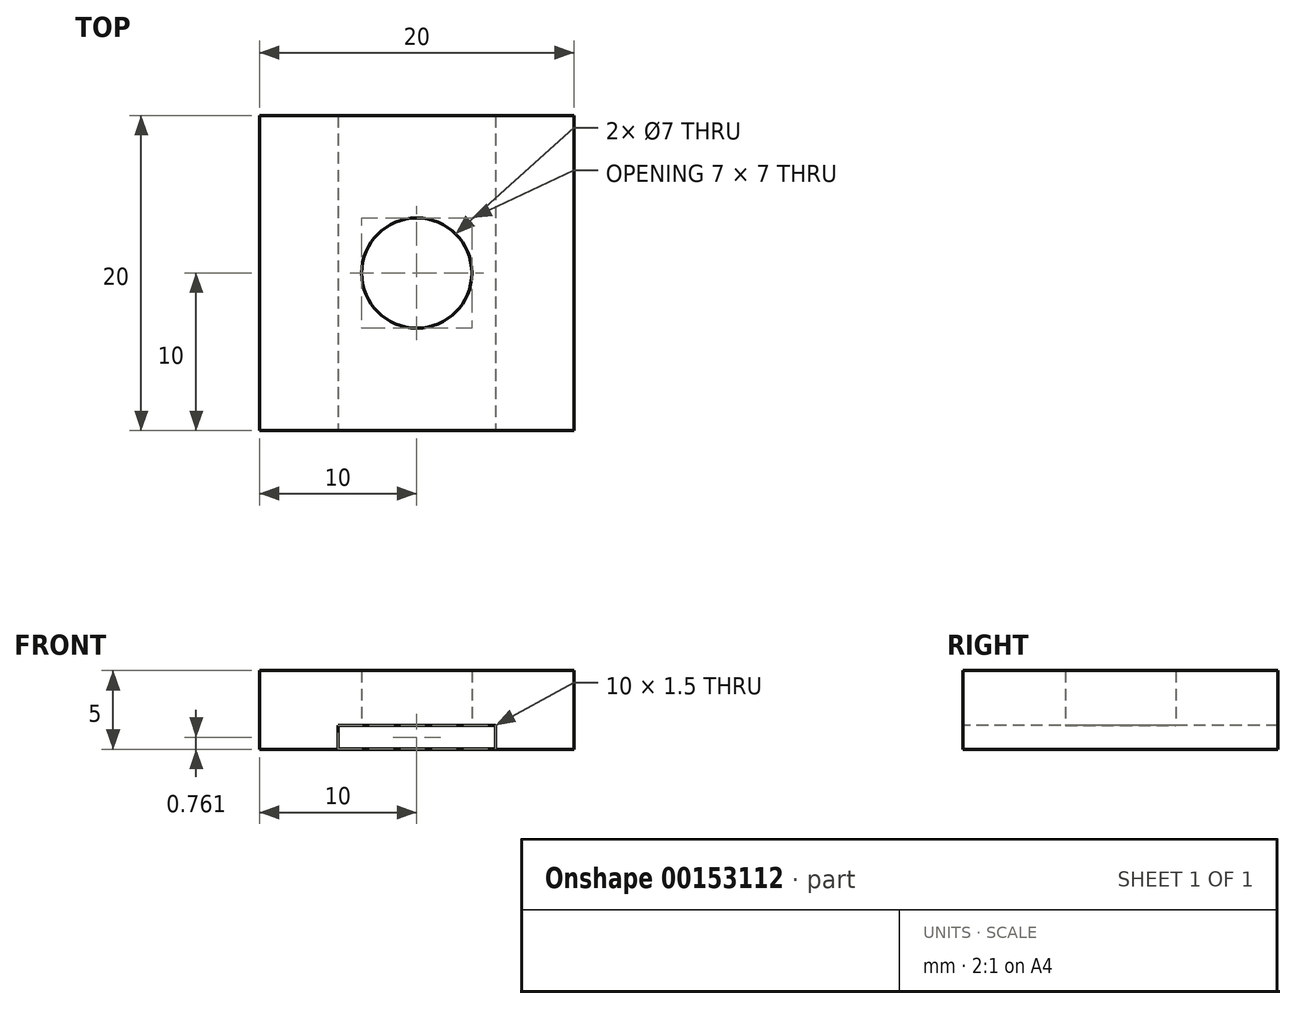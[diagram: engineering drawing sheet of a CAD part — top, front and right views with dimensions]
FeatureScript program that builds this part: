
annotation { "Feature Type Name" : "Feature", "Feature Type Description" : "" }
export const myFeature = defineFeature(function(context is Context, id is Id, definition is map)
    precondition{}
    {
        {
            var Q0;
            Q0=qCreatedBy(makeId("Top.planeOp"),FACE);
            var sketch = newSketch(context, id + "F0", { "sketchPlane" : qUnion([Q0])});
            skLineSegment(sketch, "E0.bottom", {"start": v(10, 10) * mm, "end": v(-10, 10) * mm});
            skLineSegment(sketch, "E0.top", {"start": v(10, -10) * mm, "end": v(-10, -10) * mm});
            skLineSegment(sketch, "E0.left", {"start": v(10, 10) * mm, "end": v(10, -10) * mm});
            skLineSegment(sketch, "E0.right", {"start": v(-10, 10) * mm, "end": v(-10, -10) * mm});
            skPoint(sketch, "E0.middle", {"position": v(0, 0) * mm});
            skCircle(sketch, "E1", {"center": v(0, 0) * mm, "radius": 3.5 * mm});
            skPoint(sketch, "E2.middle", {"position": v(-4.94, -0.27) * mm});
            skPoint(sketch, "E2.bottom.end.orphan", {"position": v(-4.44, 0.73) * mm});
            skPoint(sketch, "E2.top.end.orphan", {"position": v(-4.44, -1.27) * mm});
            skPoint(sketch, "E2.left.end.orphan", {"position": v(-5.44, -1.27) * mm});
            skPoint(sketch, "E2.left.start.orphan", {"position": v(-5.44, 0.73) * mm});
            skSolve(sketch);
        }
        {
            var Q0;
            Q0=makeQuery(id+"F0.imprint","IMPRINT",FACE,{"disambiguationData":[TD([[makeQuery(id+"F0.imprint","IMPRINT",EDGE,{"derivedFrom":sQuery(id+"F0.wireOp",EDGE,"E0.bottom")}),1.0]])]});
            var Q1;
            Q1=makeQuery(id+"F0.imprint","IMPRINT",FACE,{"disambiguationData":[TD([[makeQuery(id+"F0.imprint","IMPRINT",EDGE,{"derivedFrom":sQuery(id+"F0.wireOp",EDGE,"E2.bottom")}),-1.0]])]});
            extrude(context, id + "F1", {"entities" : qUnion([Q0, Q1]), "depth" : 5 * mm});
        }
        {
            var Q0;
            Q0=qCreatedBy(makeId("Front.planeOp"),FACE);
            var sketch = newSketch(context, id + "F2", { "sketchPlane" : qUnion([Q0])});
            skLineSegment(sketch, "E3.bottom", {"start": v(-5, 1.51) * mm, "end": v(5, 1.51) * mm});
            skLineSegment(sketch, "E3.top", {"start": v(-5, 0.01) * mm, "end": v(5, 0.01) * mm});
            skLineSegment(sketch, "E3.left", {"start": v(-5, 1.51) * mm, "end": v(-5, 0.01) * mm});
            skLineSegment(sketch, "E3.right", {"start": v(5, 1.51) * mm, "end": v(5, 0.01) * mm});
            skPoint(sketch, "E3.middle", {"position": v(0, 0.76) * mm});
            skSolve(sketch);
        }
        {
            var Q0;
            Q0=makeQuery(id+"F2.imprint","IMPRINT",FACE,{"disambiguationData":[TD([[makeQuery(id+"F2.imprint","IMPRINT",EDGE,{"derivedFrom":sQuery(id+"F2.wireOp",EDGE,"E3.bottom")}),-1.0]])]});
            var Q1;
            Q1=sQuery(id+"F2.wireOp",EDGE,"E3.bottom");
            extrude(context, id + "F3", {"entities" : qUnion([Q0]), "operationType" : NewBodyOperationType.REMOVE, "surfaceEntities" : qUnion([Q1]), "endBound" : BoundingType.SYMMETRIC, "oppositeDirection" : true, "depth" : 25 * mm});
        }
    });
